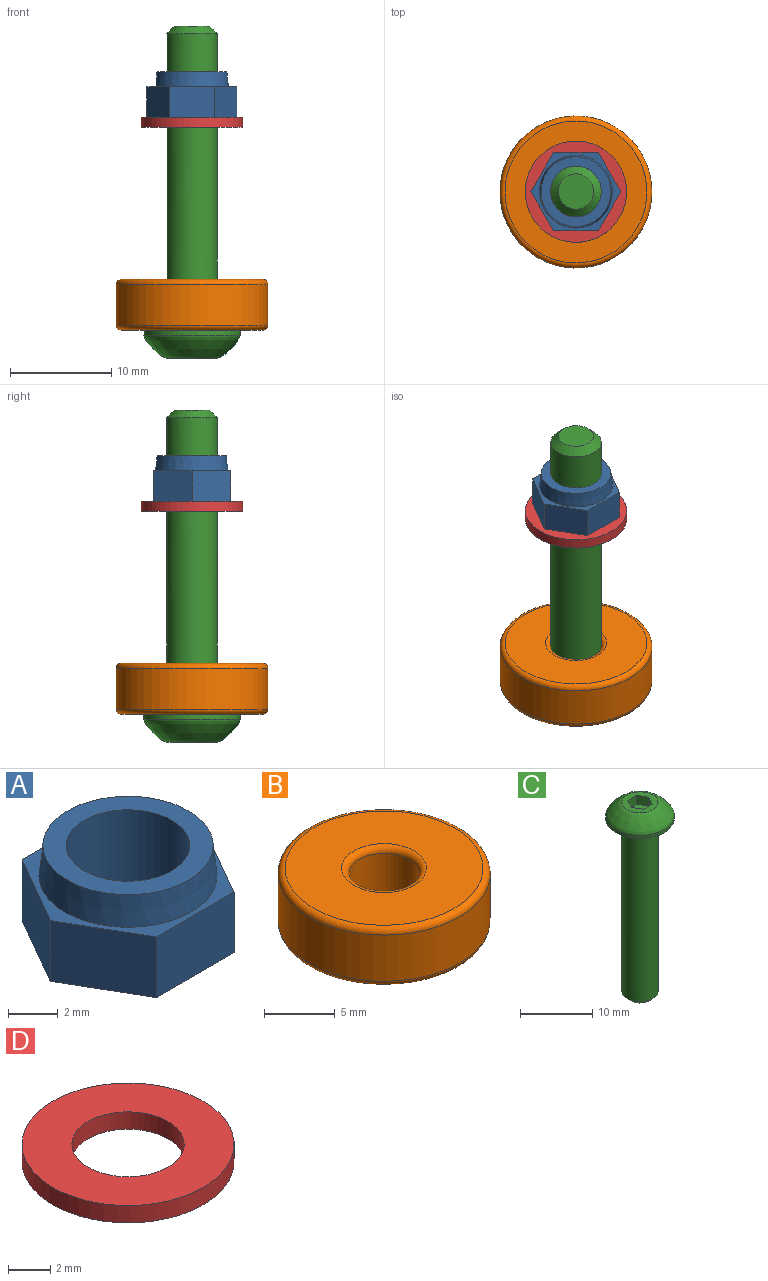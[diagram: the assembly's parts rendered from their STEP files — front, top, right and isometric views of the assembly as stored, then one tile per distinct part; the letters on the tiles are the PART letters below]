
ASSEMBLY  parts=4 mates=3
PART A: 11 faces, bbox 8.9x7.7x4.5 mm
  f0: plane 3.84x3mm, normal (-0.87,0.5,0), area 13.3mm2, adj f1,f5,f6,f7
  f1: plane 3.84x3mm, normal (-0.87,-0.5,0), area 13.3mm2, adj f0,f2,f6,f7
  f2: plane 4.43x3mm, normal (0,-1,0), area 13.3mm2, adj f1,f3,f6,f7
  f3: plane 3.84x3mm, normal (0.87,-0.5,0), area 13.3mm2, adj f2,f4,f6,f7
  f4: plane 3.84x3mm, normal (0.87,0.5,0), area 13.3mm2, adj f3,f5,f6,f7
  f5: plane 4.43x3mm, normal (0,1,0), area 13.3mm2, adj f0,f4,f6,f7
  f6: plane 8.87x7.68mm, normal (0,0,1), area 10.4mm2, adj f0,f1,f2,f3,f4,f5,f8
  f7: plane 8.87x7.68mm, normal (0,0,-1), area 31.4mm2, adj f0,f1,f2,f3,f4,f5,f10
  f8: cone r=3.6mm half-angle=6deg, axis (0,0,-1), area 33.4mm2, adj f6,f9
  f9: plane 6.88x6.88mm, normal (0,0,1), area 17.6mm2, adj f8,f10
  f10: cylinder r=2.5mm len=5mm, axis (0,0,1), area 70.7mm2, adj f7,f9
PART B: 8 faces, bbox 16.2x16.2x5 mm
  f0: cylinder r=2.5mm len=5mm, axis (0,0,-1), area 62.8mm2, adj f4,f6
  f1: cylinder r=7.5mm len=15mm, axis (0,0,-1), area 188.5mm2, adj f5,f7
  f2: plane 14x14mm, normal (0,0,1), area 125.7mm2, adj f6,f7
  f3: plane 14x14mm, normal (0,0,-1), area 125.7mm2, adj f4,f5
  f4: torus R=3mm, axis (0,0,1), area 13.2mm2, adj f0,f3
  f5: torus R=7mm, axis (0,0,1), area 36.1mm2, adj f1,f3
  f6: torus R=3mm, axis (0,0,1), area 13.2mm2, adj f0,f2
  f7: torus R=7mm, axis (0,0,1), area 36.1mm2, adj f1,f2
PART C: 14 faces, bbox 9.5x9.5x32.8 mm
  f0: plane 5.01x5.01mm, normal (0,0,1), area 11.8mm2, adj f3,f4,f5,f6,f7,f8,f10
  f1: cylinder r=4.75mm len=9.5mm, axis (0,0,-1), area 14.9mm2, adj f2,f10
  f2: plane 9.5x9.5mm, normal (0,0,-1), area 51.2mm2, adj f1,f11
  f3: plane 1.5x1.5mm, normal (-0.87,-0.5,0), area 2.6mm2, adj f0,f4,f8,f9
  f4: plane 1.73x1.5mm, normal (0,-1,0), area 2.6mm2, adj f0,f3,f5,f9
  f5: plane 1.5x1.5mm, normal (0.87,-0.5,0), area 2.6mm2, adj f0,f4,f6,f9
  f6: plane 1.5x1.5mm, normal (0.87,0.5,0), area 2.6mm2, adj f0,f5,f7,f9
  f7: plane 1.73x1.5mm, normal (0,1,0), area 2.6mm2, adj f0,f6,f8,f9
  f8: plane 1.5x1.5mm, normal (-0.87,0.5,0), area 2.6mm2, adj f0,f3,f7,f9
  f9: plane 3.46x3mm, normal (0,0,1), area 7.8mm2, adj f3,f4,f5,f6,f7,f8
  f10: bspline ~9.5x9.5mm, area 78.3mm2, adj f0,f1
  f11: cylinder r=2.5mm len=29.25mm, axis (0,0,1), area 459.5mm2, adj f2,f13
  f12: plane 3.5x3.5mm, normal (0,0,-1), area 9.6mm2, adj f13
  f13: cone r=1.75mm half-angle=45deg, axis (0,0,1), area 14.2mm2, adj f11,f12
PART D: 4 faces, bbox 10x10x1 mm
  f0: cylinder r=2.65mm len=5.3mm, axis (0,0,-1), area 16.7mm2, adj f2,f3
  f1: cylinder r=5mm len=10mm, axis (0,0,-1), area 31.4mm2, adj f2,f3
  f2: plane 10x10mm, normal (0,0,1), area 56.5mm2, adj f0,f1
  f3: plane 10x10mm, normal (0,0,-1), area 56.5mm2, adj f0,f1
PLACE A t=(-13.81,-6.82,11.96)mm
PLACE B rot(axis=(1,0,0),180deg) t=(-13.81,-6.82,-4.04)mm
PLACE C rot(axis=(1,0,0),180deg) t=(48.69,-6.82,-9.04)mm
PLACE D t=(-13.81,-6.82,10.96)mm
MATE fastened B.f0 <-> D.f0  axis (0,0,1) through (-13.81,-6.82,-4.04)mm
MATE fastened D.f0 <-> A.f8  axis (0,0,1) through (-13.81,-6.82,11.96)mm
MATE fastened C.f1 <-> B.f0  axis (0,0,1) through (-13.81,-6.82,-9.04)mm
